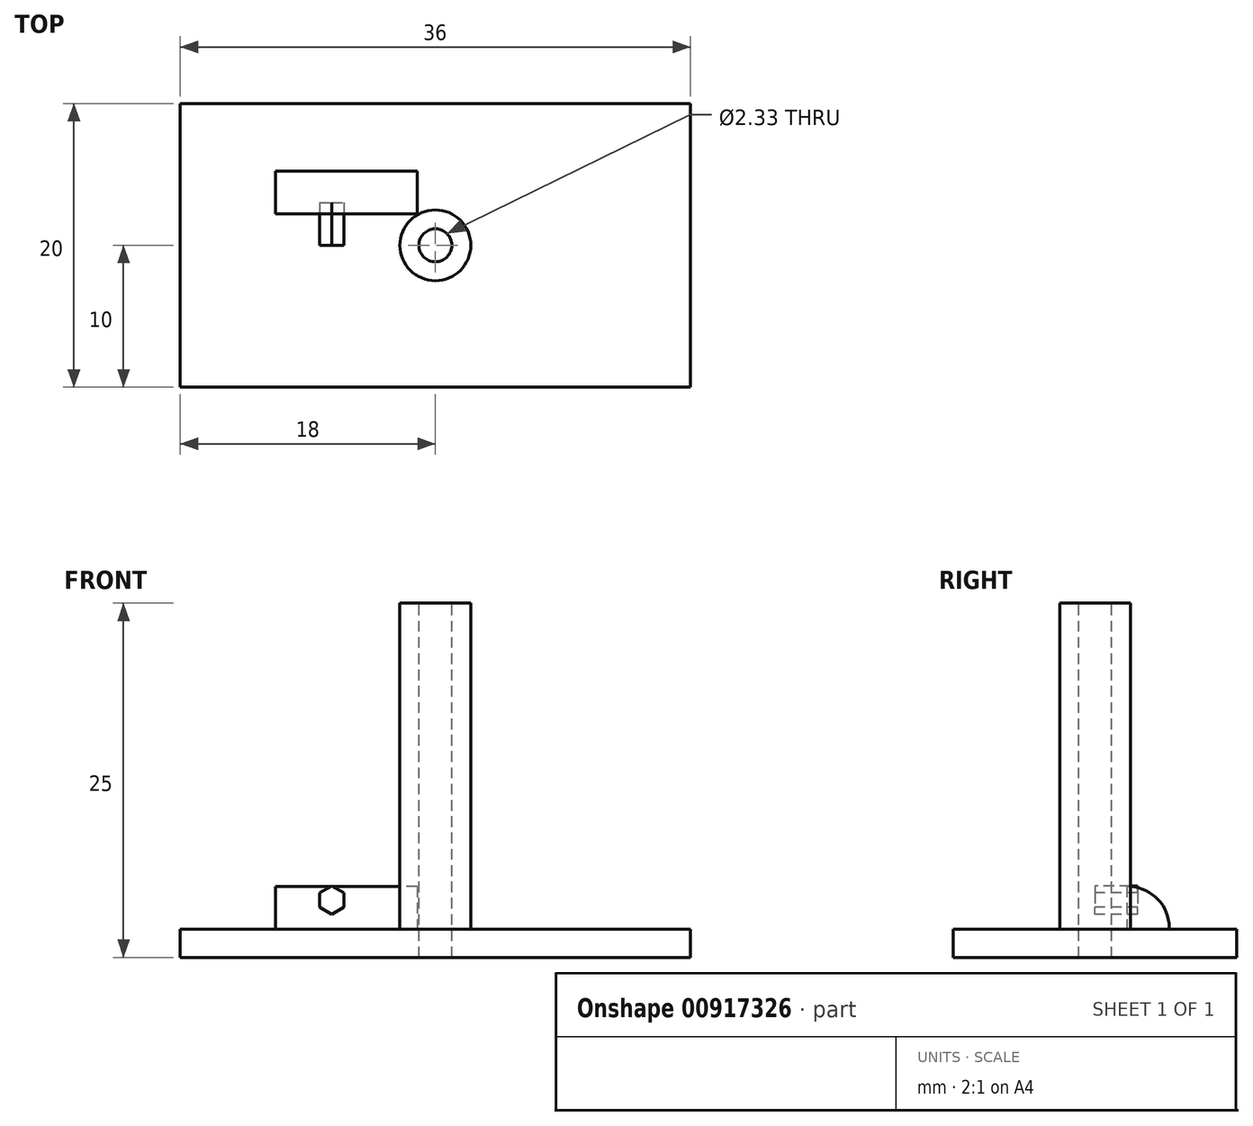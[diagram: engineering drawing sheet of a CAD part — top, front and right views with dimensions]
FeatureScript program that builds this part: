
annotation { "Feature Type Name" : "Feature", "Feature Type Description" : "" }
export const myFeature = defineFeature(function(context is Context, id is Id, definition is map)
    precondition{}
    {
        {
            var Q0;
            Q0=qCreatedBy(makeId("Top.planeOp"),FACE);
            var sketch = newSketch(context, id + "F0", { "sketchPlane" : qUnion([Q0])});
            skLineSegment(sketch, "E0.bottom", {"start": v(18, 10) * mm, "end": v(-18, 10) * mm});
            skLineSegment(sketch, "E0.top", {"start": v(18, -10) * mm, "end": v(-18, -10) * mm});
            skLineSegment(sketch, "E0.left", {"start": v(18, 10) * mm, "end": v(18, -10) * mm});
            skLineSegment(sketch, "E0.right", {"start": v(-18, 10) * mm, "end": v(-18, -10) * mm});
            skPoint(sketch, "E0.middle", {"position": v(0, 0) * mm});
            skSolve(sketch);
        }
        {
            var Q0;
            Q0=qCreatedBy(makeId("Top.planeOp"),FACE);
            var sketch = newSketch(context, id + "F1", { "sketchPlane" : qUnion([Q0])});
            skLineSegment(sketch, "E1.bottom", {"start": v(-1.28, 2.23) * mm, "end": v(-11.28, 2.23) * mm});
            skLineSegment(sketch, "E1.top", {"start": v(-1.28, 5.23) * mm, "end": v(-11.28, 5.23) * mm});
            skLineSegment(sketch, "E1.left", {"start": v(-1.28, 2.23) * mm, "end": v(-1.28, 5.23) * mm});
            skLineSegment(sketch, "E1.right", {"start": v(-11.28, 2.23) * mm, "end": v(-11.28, 5.23) * mm});
            skPoint(sketch, "E1.middle", {"position": v(-6.28, 3.73) * mm});
            skSolve(sketch);
        }
        {
            var Q0;
            Q0 = qSketchRegion(id + "F0", true);
            extrude(context, id + "F2", {"entities" : qUnion([Q0]), "depth" : 2 * mm, "offsetDistance" : 25 * mm});
        }
        {
            var Q0;
            Q0 = qSketchRegion(id + "F1", true);
            extrude(context, id + "F3", {"entities" : qUnion([Q0]), "operationType" : NewBodyOperationType.ADD, "depth" : 5 * mm, "offsetDistance" : 25 * mm});
        }
        {
            var Q0;
            Q0=makeQuery(id+"F3.opExtrude","CAP_EDGE",EDGE,{"disambiguationData":[OSD([sQuery(id+"F1.wireOp",EDGE,"E1.top")])],"isStart":false});
            fillet(context, id + "F4", {"entities" : qUnion([Q0]), "radius" : 2.9 * mm, "tangentPropagation" : true, "allowEdgeOverflow" : false});
        }
        {
            var Q0;
            Q0=qCreatedBy(makeId("Front.planeOp"),FACE);
            var sketch = newSketch(context, id + "F5", { "sketchPlane" : qUnion([Q0])});
            skCircle(sketch, "E2.cCircle", {"center": v(-7.3, 4.04) * mm, "radius": 0.87 * mm, "construction": true});
            skLineSegment(sketch, "E2.0", {"start": v(-6.44, 4.54) * mm, "end": v(-6.44, 3.54) * mm});
            skLineSegment(sketch, "E2.1", {"start": v(-6.44, 3.54) * mm, "end": v(-7.3, 3.04) * mm});
            skLineSegment(sketch, "E2.2", {"start": v(-7.3, 3.04) * mm, "end": v(-8.17, 3.54) * mm});
            skLineSegment(sketch, "E2.3", {"start": v(-8.17, 3.54) * mm, "end": v(-8.17, 4.54) * mm});
            skLineSegment(sketch, "E2.4", {"start": v(-8.17, 4.54) * mm, "end": v(-7.3, 5.04) * mm});
            skLineSegment(sketch, "E2.5", {"start": v(-7.3, 5.04) * mm, "end": v(-6.44, 4.54) * mm});
            skPoint(sketch, "E2.0.midPoint", {"position": v(-6.44, 4.04) * mm});
            skSolve(sketch);
        }
        {
            var Q0;
            Q0 = qSketchRegion(id + "F5", true);
            extrude(context, id + "F6", {"entities" : qUnion([Q0]), "oppositeDirection" : true, "depth" : 3 * mm, "offsetDistance" : 25 * mm});
        }
        {
            var Q0;
            Q0=qCreatedBy(makeId("Top.planeOp"),FACE);
            var sketch = newSketch(context, id + "F7", { "sketchPlane" : qUnion([Q0])});
            skCircle(sketch, "E3", {"center": v(0, 0) * mm, "radius": 2.5 * mm});
            skSolve(sketch);
        }
        {
            var Q0;
            Q0 = qSketchRegion(id + "F7", true);
            extrude(context, id + "F8", {"entities" : qUnion([Q0]), "operationType" : NewBodyOperationType.ADD, "depth" : 25 * mm, "offsetDistance" : 25 * mm});
        }
        {
            var Q0;
            Q0=makeQuery(id+"F8.opExtrude","CAP_FACE",FACE,{"disambiguationData":[OSD([sQuery(id+"F7.wireOp",EDGE,"E3")])],"isStart":false});
            var sketch = newSketch(context, id + "F9", { "sketchPlane" : qUnion([Q0])});
            skCircle(sketch, "E4", {"center": v(0, 0) * mm, "radius": 1.16 * mm});
            skSolve(sketch);
        }
        {
            var Q0;
            Q0 = qSketchRegion(id + "F9", true);
            extrude(context, id + "F10", {"entities" : qUnion([Q0]), "operationType" : NewBodyOperationType.REMOVE, "oppositeDirection" : true, "depth" : 30 * mm, "offsetDistance" : 25 * mm});
        }
    });
